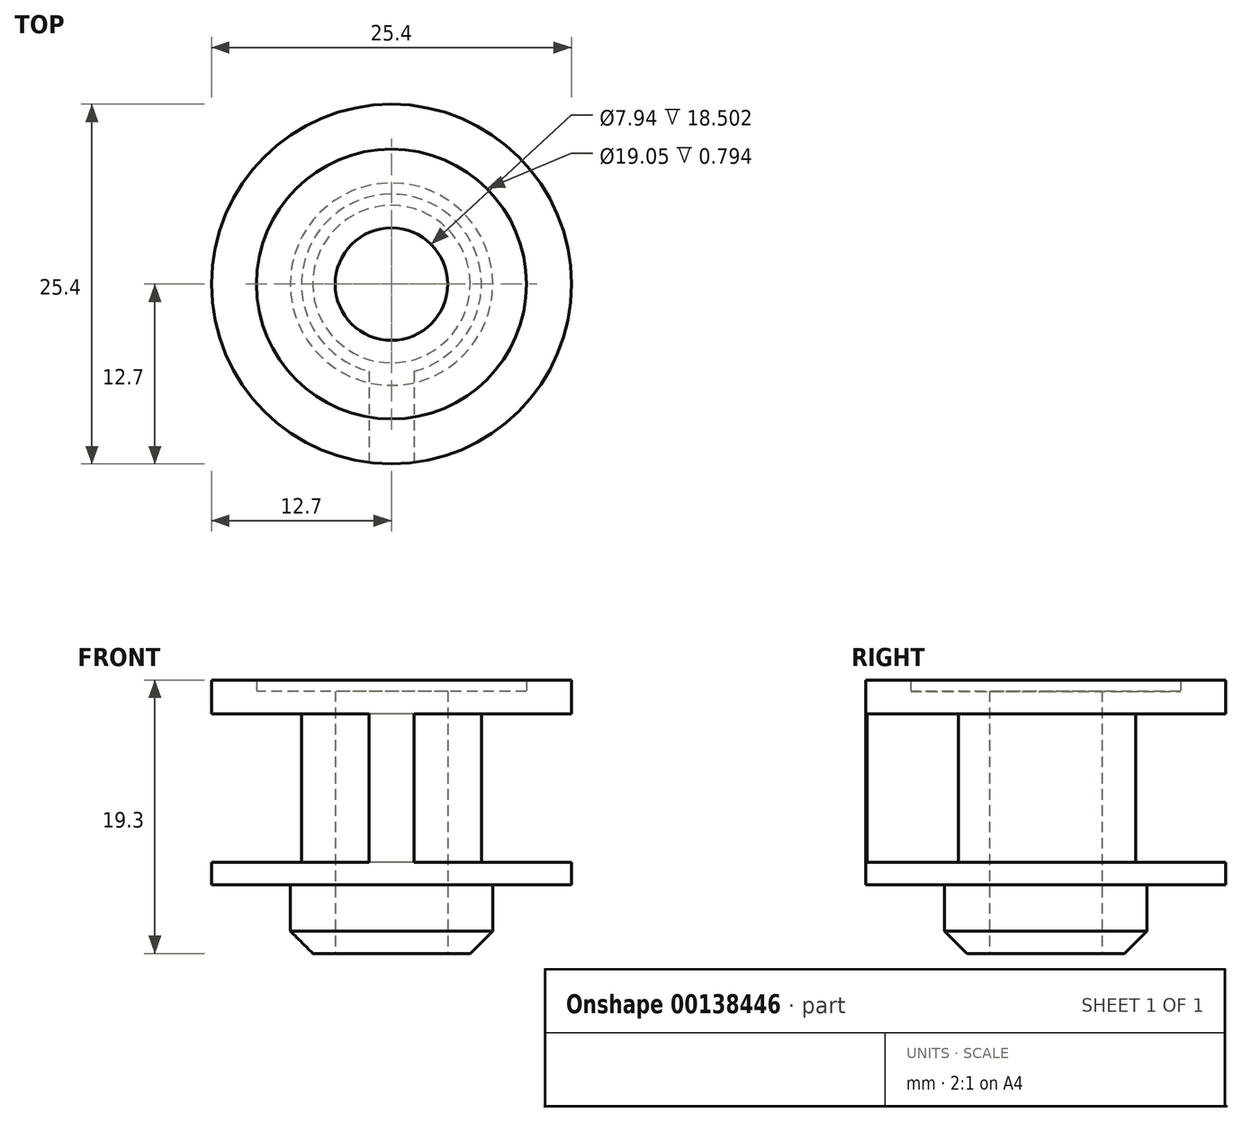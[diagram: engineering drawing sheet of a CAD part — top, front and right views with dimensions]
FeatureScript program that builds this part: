
annotation { "Feature Type Name" : "Feature", "Feature Type Description" : "" }
export const myFeature = defineFeature(function(context is Context, id is Id, definition is map)
    precondition{}
    {
        {
            var Q0;
            Q0=qCreatedBy(makeId("Top.planeOp"),FACE);
            var sketch = newSketch(context, id + "F0", { "sketchPlane" : qUnion([Q0])});
            skCircle(sketch, "E0", {"center": v(0, 0) * mm, "radius": 12.7 * mm});
            skCircle(sketch, "E1", {"center": v(0, 0) * mm, "radius": 3.97 * mm});
            skSolve(sketch);
        }
        {
            var Q0;
            Q0=qSketchRegion(id+"F0",true);
            extrude(context, id + "F1", {"entities" : qUnion([Q0]), "depth" : 1.59 * mm});
        }
        {
            var Q0;
            Q0=makeQuery(id+"F1.opExtrude","CAP_FACE",FACE,{"disambiguationData":[OSD([sQuery(id+"F0.wireOp",EDGE,"E0")])],"isStart":true});
            var sketch = newSketch(context, id + "F2", { "sketchPlane" : qUnion([Q0])});
            skCircle(sketch, "E2", {"center": v(0, 0) * mm, "radius": 12.7 * mm});
            skCircle(sketch, "E3", {"center": v(0, 0) * mm, "radius": 9.53 * mm});
            skSolve(sketch);
        }
        {
            var Q0;
            Q0=qSketchRegion(id+"F2",true);
            extrude(context, id + "F3", {"entities" : qUnion([Q0]), "operationType" : NewBodyOperationType.ADD, "depth" : 1 / 812.8 * mm});
        }
        {
            var Q0;
            Q0=makeQuery(id+"F1.opExtrude","CAP_FACE",FACE,{"disambiguationData":[OSD([sQuery(id+"F0.wireOp",EDGE,"E0"),sQuery(id+"F0.wireOp",EDGE,"E1")])],"isStart":false});
            var sketch = newSketch(context, id + "F4", { "sketchPlane" : qUnion([Q0])});
            skCircle(sketch, "E4", {"center": v(0, 0) * mm, "radius": 3.97 * mm});
            skCircle(sketch, "E5", {"center": v(0, 0) * mm, "radius": 6.35 * mm});
            skSolve(sketch);
        }
        {
            var Q0;
            Q0=qSketchRegion(id+"F4",true);
            extrude(context, id + "F5", {"entities" : qUnion([Q0]), "operationType" : NewBodyOperationType.ADD, "depth" : 10.47 * mm});
        }
        {
            var Q0;
            Q0=makeQuery(id+"F5.opExtrude","CAP_FACE",FACE,{"disambiguationData":[OSD([sQuery(id+"F4.wireOp",EDGE,"E4"),sQuery(id+"F4.wireOp",EDGE,"E5")])],"isStart":false});
            var sketch = newSketch(context, id + "F6", { "sketchPlane" : qUnion([Q0])});
            skCircle(sketch, "E6", {"center": v(0, 0) * mm, "radius": 12.7 * mm});
            skCircle(sketch, "E7", {"center": v(0, 0) * mm, "radius": 3.97 * mm});
            skSolve(sketch);
        }
        {
            var Q0;
            Q0=qSketchRegion(id+"F6",true);
            extrude(context, id + "F7", {"entities" : qUnion([Q0]), "operationType" : NewBodyOperationType.ADD, "depth" : 1.59 * mm});
        }
        {
            var Q0;
            Q0=makeQuery(id+"F7.opExtrude","CAP_FACE",FACE,{"disambiguationData":[OSD([sQuery(id+"F6.wireOp",EDGE,"E6"),sQuery(id+"F6.wireOp",EDGE,"E7")])],"isStart":false});
            var sketch = newSketch(context, id + "F8", { "sketchPlane" : qUnion([Q0])});
            skCircle(sketch, "E8", {"center": v(0, 0) * mm, "radius": 9.53 * mm});
            skCircle(sketch, "E9", {"center": v(0, 0) * mm, "radius": 12.7 * mm});
            skSolve(sketch);
        }
        {
            var Q0;
            Q0=qSketchRegion(id+"F8",true);
            extrude(context, id + "F9", {"entities" : qUnion([Q0]), "operationType" : NewBodyOperationType.ADD, "depth" : 0.8 * mm});
        }
        {
            var Q0;
            Q0=makeQuery(id+"F1.opExtrude","CAP_FACE",FACE,{"disambiguationData":[OSD([sQuery(id+"F0.wireOp",EDGE,"E0"),sQuery(id+"F0.wireOp",EDGE,"E1")])],"isStart":false});
            var sketch = newSketch(context, id + "F10", { "sketchPlane" : qUnion([Q0])});
            skLineSegment(sketch, "E10", {"start": v(0, 0) * mm, "end": v(0, -9.37) * mm, "construction": true});
            skLineSegment(sketch, "E11", {"start": v(-1.59, -9.37) * mm, "end": v(1.59, -9.37) * mm, "construction": true});
            skLineSegment(sketch, "E12", {"start": v(1.59, -6.15) * mm, "end": v(1.59, -12.6) * mm});
            skLineSegment(sketch, "E13", {"start": v(-1.59, -6.15) * mm, "end": v(-1.59, -12.6) * mm});
            skArc(sketch, "E14", {"start": v(-1.59, -12.6) * mm, "mid": v(0, -12.7) * mm, "end": v(1.59, -12.6) * mm});
            skArc(sketch, "E15", {"start": v(-1.59, -6.15) * mm, "mid": v(0, -6.35) * mm, "end": v(1.59, -6.15) * mm});
            skSolve(sketch);
        }
        {
            var Q0;
            Q0=qSketchRegion(id+"F10",true);
            var Q1;
            Q1=makeQuery(id+"F7.opExtrude","CAP_FACE",FACE,{"disambiguationData":[OSD([sQuery(id+"F6.wireOp",EDGE,"E6"),sQuery(id+"F6.wireOp",EDGE,"E7")])],"isStart":true});
            extrude(context, id + "F11", {"entities" : qUnion([Q0]), "operationType" : NewBodyOperationType.ADD, "endBound" : BoundingType.UP_TO_SURFACE, "endBoundEntityFace" : qUnion([Q1]), "depth" : 25.4 * mm});
        }
        {
            var Q0;
            Q0=makeQuery(id+"F1.opExtrude","CAP_FACE",FACE,{"disambiguationData":[OSD([sQuery(id+"F0.wireOp",EDGE,"E0"),sQuery(id+"F0.wireOp",EDGE,"E1")])],"isStart":true});
            var sketch = newSketch(context, id + "F12", { "sketchPlane" : qUnion([Q0])});
            skCircle(sketch, "E16", {"center": v(0, 0) * mm, "radius": 3.97 * mm});
            skCircle(sketch, "E17", {"center": v(0, 0) * mm, "radius": 7.14 * mm});
            skSolve(sketch);
        }
        {
            var Q0;
            Q0=qSketchRegion(id+"F12",true);
            extrude(context, id + "F13", {"entities" : qUnion([Q0]), "operationType" : NewBodyOperationType.ADD, "depth" : 4.86 * mm});
        }
        {
            var Q0;
            Q0=makeQuery(id+"F13.opExtrude","CAP_EDGE",EDGE,{"disambiguationData":[OSD([sQuery(id+"F12.wireOp",EDGE,"E17")])],"isStart":false});
            chamfer(context, id + "F14", {"entities" : qUnion([Q0]), "width" : 1.59 * mm, "tangentPropagation" : true});
        }
    });
